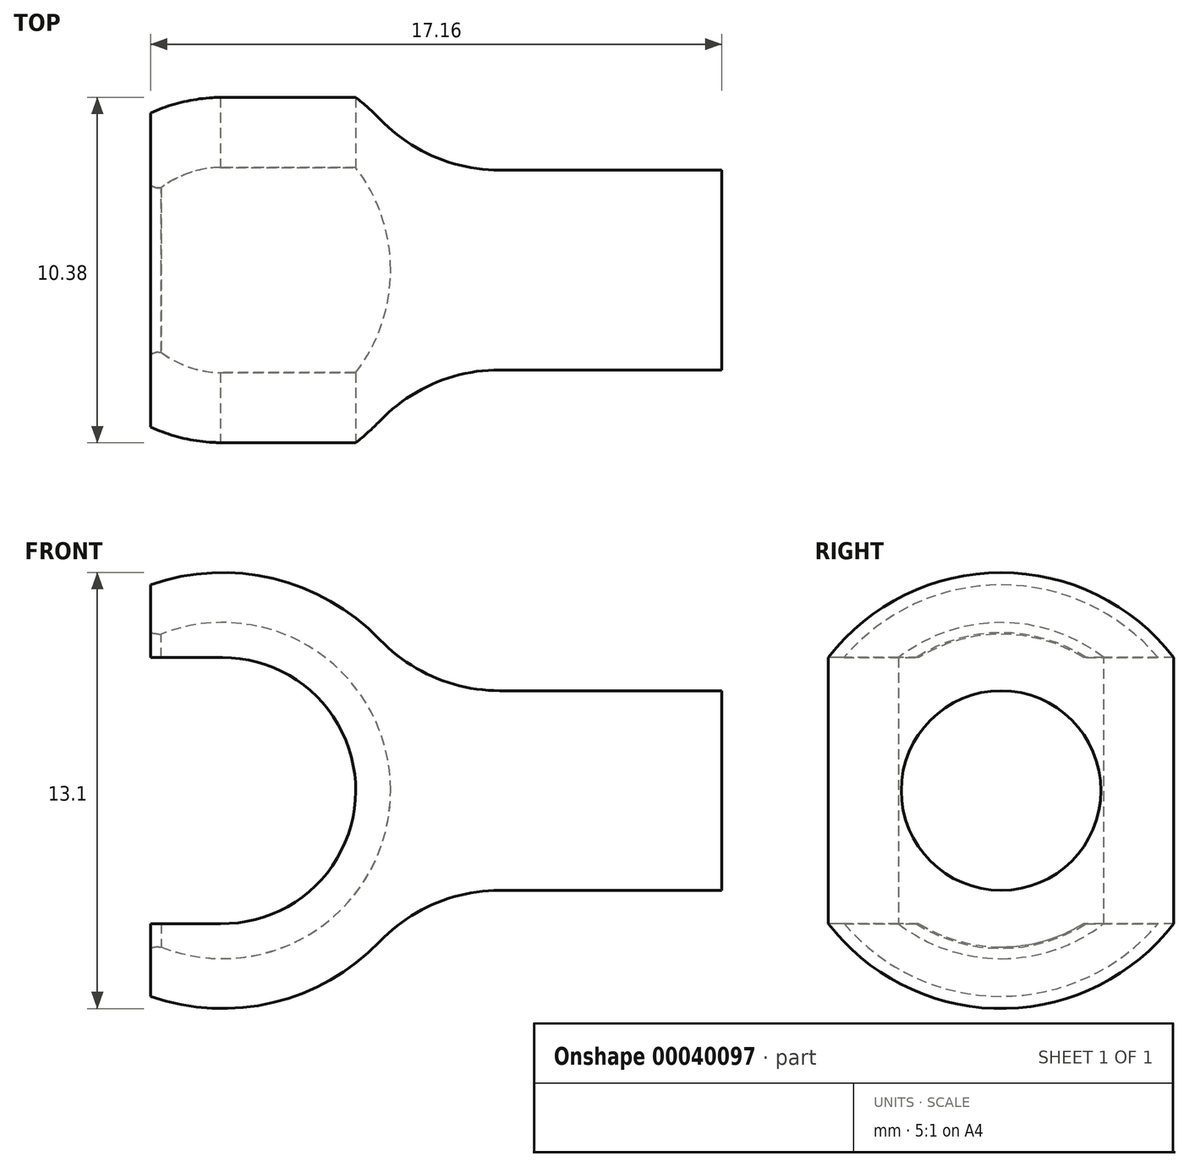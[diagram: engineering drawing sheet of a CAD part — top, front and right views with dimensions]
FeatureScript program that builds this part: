
annotation { "Feature Type Name" : "Feature", "Feature Type Description" : "" }
export const myFeature = defineFeature(function(context is Context, id is Id, definition is map)
    precondition{}
    {
        {
            var Q0;
            Q0=qCreatedBy(makeId("Front.planeOp"),FACE);
            var sketch = newSketch(context, id + "F0", { "sketchPlane" : qUnion([Q0])});
            skLineSegment(sketch, "E0", {"start": v(0, 0) * mm, "end": v(-9.95, 0) * mm});
            skLineSegment(sketch, "E1", {"start": v(0, 0) * mm, "end": v(0, -3) * mm});
            skLineSegment(sketch, "E2.0", {"start": v(0, -3) * mm, "end": v(-9.18, -3) * mm});
            skArc(sketch, "E3.trimOffspring", {"start": v(-17.16, -6.18) * mm, "mid": v(-12.58, -6.08) * mm, "end": v(-9.18, -3) * mm});
            skArc(sketch, "E4.trimOffspring", {"start": v(-16.85, -4.7) * mm, "mid": v(-12.16, -4.17) * mm, "end": v(-9.95, 0) * mm});
            skLineSegment(sketch, "E5.trimOffspring", {"start": v(-16.85, -4.7) * mm, "end": v(-16.91, -4.7) * mm});
            skPoint(sketch, "E6.visualSharp", {"position": v(-19.56, -4.7) * mm});
            skArc(sketch, "E6.filletArc", {"start": v(-16.91, -4.7) * mm, "mid": v(-17.04, -4.71) * mm, "end": v(-17.16, -4.74) * mm});
            skLineSegment(sketch, "E7", {"start": v(-17.16, -6.18) * mm, "end": v(-17.16, -4.74) * mm});
            skSolve(sketch);
        }
        {
            var Q0;
            Q0 = qSketchRegion(id + "F0", true);
            var Q1;
            Q1=sQuery(id+"F0.wireOp",EDGE,"E0");
            revolve(context, id + "F1", {"entities" : qUnion([Q0]), "axis" : qUnion([Q1]), "revolveType" : RevolveType.FULL});
        }
        {
            var Q0;
            Q0=qCreatedBy(makeId("Front.planeOp"),FACE);
            var sketch = newSketch(context, id + "F2", { "sketchPlane" : qUnion([Q0])});
            skPoint(sketch, "E8.center.orphan", {"position": v(-13.79, 0) * mm});
            skArc(sketch, "E9", {"start": v(-15.06, -4) * mm, "mid": v(-11, -0.03) * mm, "end": v(-15, 4) * mm});
            skLineSegment(sketch, "E10", {"start": v(-15.06, -4) * mm, "end": v(-18.56, -4) * mm});
            skLineSegment(sketch, "E11", {"start": v(-15, 4) * mm, "end": v(-18.58, 4) * mm});
            skPoint(sketch, "E12.orphan", {"position": v(-15, 5.07) * mm});
            skLineSegment(sketch, "E13", {"start": v(-18.58, 4) * mm, "end": v(-18.56, -4) * mm});
            skPoint(sketch, "E13.endSnap0", {"position": v(-19.2, -4) * mm});
            skPoint(sketch, "E14.orphan", {"position": v(-22.15, 3.99) * mm});
            skPoint(sketch, "E15.orphan", {"position": v(-23.34, -4) * mm});
            skSolve(sketch);
        }
        {
            var Q0;
            Q0 = qSketchRegion(id + "F2", true);
            extrude(context, id + "F3", {"entities" : qUnion([Q0]), "operationType" : NewBodyOperationType.REMOVE, "endBound" : BoundingType.SYMMETRIC, "oppositeDirection" : true, "depth" : 25 * mm});
        }
        {
            var Q0;
            Q0=makeQuery(id+"F1.opRevolve","SWEPT_EDGE",EDGE,{"disambiguationData":[OSD([sQuery(id+"F0.wireOp",EDGE,"E2.0"),sQuery(id+"F0.wireOp",EDGE,"E3.trimOffspring")])]});
            fillet(context, id + "F4", {"entities" : qUnion([Q0]), "radius" : 5 * mm, "tangentPropagation" : true, "allowEdgeOverflow" : false});
        }
    });
